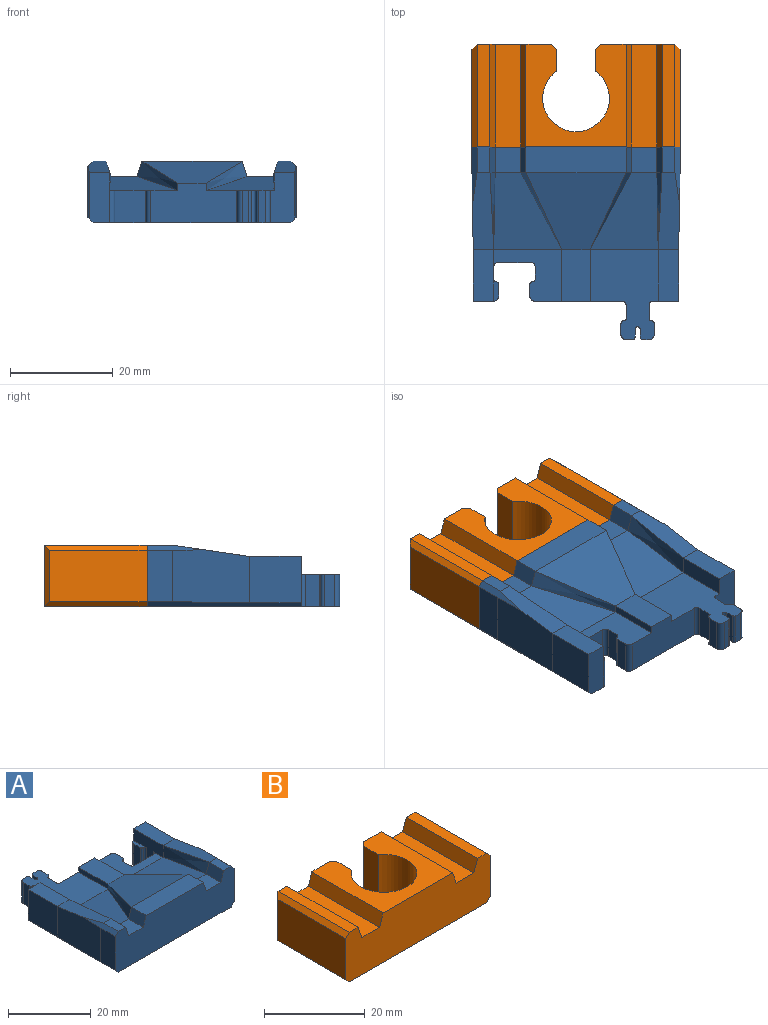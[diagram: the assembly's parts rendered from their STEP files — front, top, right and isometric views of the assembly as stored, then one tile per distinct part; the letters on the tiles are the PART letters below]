
ASSEMBLY  parts=2 mates=1
PART A: 75 faces, bbox 40.5x37.5x12 mm
  f0: plane 9.8x4mm, normal (0,1,0), area 38.9mm2, adj f1,f8,f9,f10,f35,f72
  f1: plane 38.5x37.5mm, normal (0,0,-1), area 1140.5mm2, adj f0,f3,f10,f15,f16,f17,f18,f19
  f2: plane 4.25x1mm, normal (0,0,1), area 3.5mm2, adj f10,f35,f36,f37,f38
  f3: plane 17x7.75mm, normal (0,1,0), area 115.1mm2, adj f1,f4,f11,f12,f13,f14,f16,f47
  f4: plane 17.5x13.25mm, normal (0,0,1), area 170.8mm2, adj f3,f5,f14,f15,f16,f17,f18,f19
  f5: plane 10x3.5mm, normal (1,0,0), area 35mm2, adj f4,f6,f15,f62
  f6: plane 10x4mm, normal (0,0,1), area 40mm2, adj f5,f7,f15,f61
  f7: plane 10x9.06mm, normal (-1,0,0), area 90.6mm2, adj f6,f15,f60,f71
  f8: plane 10x9.04mm, normal (1,0,0), area 90.4mm2, adj f0,f9,f70,f72
  f9: plane 10x4mm, normal (0,0,1), area 40mm2, adj f0,f8,f10,f69
  f10: plane 10x9.8mm, normal (-1,0,0), area 50.7mm2, adj f0,f1,f2,f9,f11,f38,f39,f68
  f11: plane 13.25x10mm, normal (0,0,1), area 76.1mm2, adj f3,f10,f12,f39,f40,f41,f42,f43
  f12: plane 10x1.45mm, normal (1,0,0), area 14.5mm2, adj f3,f11,f13,f66
  f13: plane 10x5.5mm, normal (0,0,1), area 55mm2, adj f3,f12,f14,f65
  f14: plane 10x1.45mm, normal (-1,0,0), area 14.5mm2, adj f3,f4,f13,f64
  f15: plane 9.8x5mm, normal (0,1,0), area 45.2mm2, adj f1,f4,f5,f6,f7,f17,f71
  f16: cylinder r=0.75mm len=6.3mm, axis (0,0,-1), area 7.4mm2, adj f1,f3,f4,f34
  f17: cylinder r=0.75mm len=6.3mm, axis (0,0,-1), area 7.4mm2, adj f1,f4,f15,f18
  f18: plane 6.3x2.75mm, normal (-1,0,0), area 17.3mm2, adj f1,f4,f17,f19
  f19: cylinder r=0.25mm len=6.3mm, axis (0,0,-1), area 2.5mm2, adj f1,f4,f18,f20
  f20: cylinder r=0.75mm len=6.3mm, axis (0,0,-1), area 7.4mm2, adj f1,f4,f19,f21
  f21: plane 6.3x2mm, normal (-1,0,0), area 12.6mm2, adj f1,f4,f20,f22
  f22: cylinder r=1mm len=6.3mm, axis (0,0,-1), area 9.9mm2, adj f1,f4,f21,f23
  f23: plane 6.3x1.25mm, normal (0,1,0), area 7.9mm2, adj f1,f4,f22,f24
  f24: cylinder r=0.5mm len=6.3mm, axis (0,0,-1), area 4.9mm2, adj f1,f4,f23,f25
  f25: plane 6.3x1.5mm, normal (1,0,0), area 9.5mm2, adj f1,f4,f24,f26
  f26: cylinder r=0.5mm len=6.3mm, axis (0,0,-1), area 9.9mm2, adj f1,f4,f25,f27
  f27: plane 6.3x1.5mm, normal (-1,0,0), area 9.5mm2, adj f1,f4,f26,f28
  f28: cylinder r=0.5mm len=6.3mm, axis (0,0,-1), area 4.9mm2, adj f1,f4,f27,f29
  f29: plane 6.3x1.25mm, normal (0,1,0), area 7.9mm2, adj f1,f4,f28,f30
  f30: cylinder r=1mm len=6.3mm, axis (0,0,-1), area 9.9mm2, adj f1,f4,f29,f31
  f31: plane 6.3x2mm, normal (1,0,0), area 12.6mm2, adj f1,f4,f30,f32
  f32: cylinder r=0.75mm len=6.3mm, axis (0,0,-1), area 7.4mm2, adj f1,f4,f31,f33
  f33: cylinder r=0.25mm len=6.3mm, axis (0,0,-1), area 2.5mm2, adj f1,f4,f32,f34
  f34: plane 6.3x2.75mm, normal (1,0,0), area 17.3mm2, adj f1,f4,f16,f33
  f35: cylinder r=1mm len=6.3mm, axis (0,0,-1), area 9.9mm2, adj f0,f1,f2,f36
  f36: plane 6.3x2.25mm, normal (-1,0,0), area 14.2mm2, adj f1,f2,f35,f37
  f37: cylinder r=0.5mm len=6.3mm, axis (0,0,-1), area 4.9mm2, adj f1,f2,f36,f38
  f38: cylinder r=0.5mm len=6.3mm, axis (0,0,-1), area 4.9mm2, adj f1,f2,f10,f37
  f39: cylinder r=0.75mm len=6.3mm, axis (0,0,-1), area 7.4mm2, adj f1,f10,f11,f40
  f40: plane 6.55x6.3mm, normal (0,1,0), area 41.3mm2, adj f1,f11,f39,f41
  f41: cylinder r=0.75mm len=6.3mm, axis (0,0,-1), area 7.4mm2, adj f1,f11,f40,f42
  f42: plane 6.3x2.5mm, normal (1,0,0), area 15.7mm2, adj f1,f11,f41,f43
  f43: cylinder r=0.5mm len=6.3mm, axis (0,0,-1), area 4.9mm2, adj f1,f11,f42,f44
  f44: plane 6.3x0.05mm, normal (0,-1,0), area 0.3mm2, adj f1,f11,f43,f45
  f45: cylinder r=0.5mm len=6.3mm, axis (0,0,-1), area 4.9mm2, adj f1,f11,f44,f46
  f46: plane 6.3x2.25mm, normal (1,0,0), area 14.2mm2, adj f1,f11,f45,f47
  f47: cylinder r=1mm len=6.3mm, axis (0,0,-1), area 9.9mm2, adj f1,f3,f11,f46
  f48: plane 10x5mm, normal (1,0,0), area 50mm2, adj f59,f70,f72,f73
  f49: plane 5x2.5mm, normal (0,0,1), area 12.5mm2, adj f50,f59,f69,f73
  f50: plane 5x3mm, normal (-0.95,0,0.32), area 15.8mm2, adj f49,f51,f59,f68
  f51: plane 5x5mm, normal (0,0,1), area 25mm2, adj f50,f52,f59,f67
  f52: plane 5x3mm, normal (0.95,0,0.32), area 15.8mm2, adj f51,f53,f59,f66
  f53: plane 19.5x5mm, normal (0,0,1), area 97.5mm2, adj f52,f54,f59,f65
  f54: plane 5x3mm, normal (-0.95,0,0.32), area 15.8mm2, adj f53,f55,f59,f64
  f55: plane 5x5mm, normal (0,0,1), area 25mm2, adj f54,f56,f59,f63
  f56: plane 5x3mm, normal (0.95,0,0.32), area 15.8mm2, adj f55,f57,f59,f62
  f57: plane 5x2.5mm, normal (0,0,1), area 12.5mm2, adj f56,f59,f61,f74
  f58: plane 10x5mm, normal (-1,0,0), area 50mm2, adj f59,f60,f71,f74
  f59: plane 40.5x12mm, normal (0,-1,0), area 448mm2, adj f1,f48,f49,f50,f51,f52,f53,f54
  f60: plane 15x10.37mm, normal (-1,0.02,0), area 147.4mm2, adj f7,f58,f61,f71,f74
  f61: plane 15x4.15mm, normal (0,0.15,0.99), area 53.8mm2, adj f6,f57,f60,f62,f74
  f62: bspline ~15x5.7mm, area 49.6mm2, adj f5,f56,f61,f63
  f63: plane 15x13.25mm, normal (0,0.18,0.98), area 139.1mm2, adj f4,f55,f62,f64
  f64: bspline ~15x8.01mm, area 39mm2, adj f14,f54,f63,f65
  f65: plane 19.5x15mm, normal (0,0.27,0.96), area 194.9mm2, adj f13,f53,f64,f66
  f66: bspline ~15x7.99mm, area 39mm2, adj f12,f52,f65,f67
  f67: plane 15x13.25mm, normal (0,0.18,0.98), area 139.1mm2, adj f11,f51,f66,f68
  f68: bspline ~15x5.7mm, area 49.6mm2, adj f10,f50,f67,f69
  f69: plane 15x4.14mm, normal (0,0.15,0.99), area 53.7mm2, adj f9,f49,f68,f70,f73
  f70: plane 15x10.34mm, normal (1,0.02,0), area 147.2mm2, adj f8,f48,f69,f72,f73
  f71: plane 30x1mm, normal (-0.71,0,-0.71), area 36mm2, adj f1,f7,f15,f58,f59,f60
  f72: plane 30x1mm, normal (0.71,0,-0.71), area 36.5mm2, adj f0,f1,f8,f48,f59,f70
  f73: plane 11.15x1mm, normal (0.71,0,0.71), area 11.4mm2, adj f48,f49,f59,f69,f70
  f74: plane 11.1x1mm, normal (-0.71,0,0.71), area 11.4mm2, adj f57,f58,f59,f60,f61
PART B: 26 faces, bbox 40.5x20x12 mm
  f0: plane 38.5x20mm, normal (0,0,-1), area 603.4mm2, adj f2,f13,f14,f15,f16,f17,f18,f21
  f1: plane 20x19.5mm, normal (0,0,1), area 223.4mm2, adj f2,f7,f8,f13,f14,f15,f16,f17
  f2: plane 14.51x12mm, normal (0,1,0), area 156.1mm2, adj f0,f1,f8,f9,f10,f11,f20,f21
  f3: plane 19x10mm, normal (1,0,0), area 190mm2, adj f14,f23,f24,f25
  f4: plane 20x2.5mm, normal (0,0,1), area 50mm2, adj f5,f13,f14,f24
  f5: plane 20x3mm, normal (-0.95,0,0.32), area 63.2mm2, adj f4,f6,f13,f14
  f6: plane 20x5mm, normal (0,0,1), area 100mm2, adj f5,f7,f13,f14
  f7: plane 20x3mm, normal (0.95,0,0.32), area 63.2mm2, adj f1,f6,f13,f14
  f8: plane 20x3mm, normal (-0.95,0,0.32), area 63.2mm2, adj f1,f2,f9,f14
  f9: plane 20x5mm, normal (0,0,1), area 100mm2, adj f2,f8,f10,f14
  f10: plane 20x3mm, normal (0.95,0,0.32), area 63.2mm2, adj f2,f9,f11,f14
  f11: plane 20x2.5mm, normal (0,0,1), area 50mm2, adj f2,f10,f14,f19
  f12: plane 19x10mm, normal (-1,0,0), area 190mm2, adj f14,f18,f19,f20
  f13: plane 14.49x12mm, normal (0,1,0), area 155.9mm2, adj f0,f1,f4,f5,f6,f7,f22,f25
  f14: plane 40.5x12mm, normal (0,-1,0), area 448mm2, adj f0,f1,f3,f4,f5,f6,f7,f8
  f15: cylinder r=6.5mm len=13mm, axis (0,0,1), area 394.2mm2, adj f0,f1,f16,f17
  f16: plane 12x4.19mm, normal (1,0,0), area 50.3mm2, adj f0,f1,f15,f21
  f17: plane 12x4.19mm, normal (-1,0,0), area 50.3mm2, adj f0,f1,f15,f22
  f18: plane 20x1mm, normal (-0.71,0,-0.71), area 27.6mm2, adj f0,f12,f14,f20
  f19: plane 20x1mm, normal (-0.71,0,0.71), area 27.6mm2, adj f11,f12,f14,f20
  f20: plane 12x1mm, normal (-0.71,0.71,0), area 15.6mm2, adj f2,f12,f18,f19
  f21: plane 12x1mm, normal (0.71,0.71,0), area 17mm2, adj f0,f1,f2,f16
  f22: plane 12x1mm, normal (-0.71,0.71,0), area 17mm2, adj f0,f1,f13,f17
  f23: plane 20x1mm, normal (0.71,0,-0.71), area 27.6mm2, adj f0,f3,f14,f25
  f24: plane 20x1mm, normal (0.71,0,0.71), area 27.6mm2, adj f3,f4,f14,f25
  f25: plane 12x1mm, normal (0.71,0.71,0), area 15.6mm2, adj f3,f13,f23,f24
PLACE A rot(axis=(0,0,-1),180deg) t=(-0.86,-25.43,1.01)mm
PLACE B t=(-0.85,4.57,1.02)mm
MATE fastened B.f14 <-> A.f59  axis (0,-1,0) through (-0.85,4.57,6.65)mm
